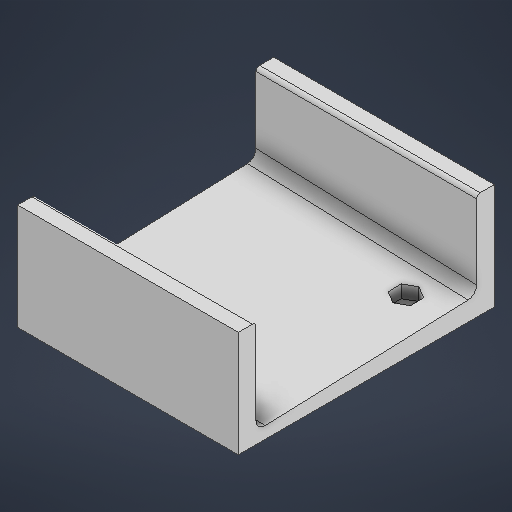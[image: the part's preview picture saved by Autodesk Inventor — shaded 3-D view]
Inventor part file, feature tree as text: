
AUTODESK INVENTOR PART (.ipt)
format: ipt  version: 2025.1 (Build 291241020, 241B)  size: 284,672 bytes
history: native  units: in
note: dims shown in document units (in); Inventor stores cm internally (conversion verified against a paired STEP export)
features: extrude x5, sketch x5, plane x2, fillet x2, projected_geometry x2
ambient origin geometry x8: Origin, YZ Plane, XZ Plane, XY Plane, X Axis, Y Axis, Z Axis, Center Point
bodies: Solid1 (feature_tree)
feature tree (16):
  extrude  "Extrusion1"  Depth=3.62in
  plane  "Work Plane3"
  sketch  "Sketch4"  dims[d2=0.125in d3=0.25in d4=0.125in]
  extrude  "Extrusion2"  Depth=0.25in
  fillet  "Fillet1"  Radius=0.125in
  plane  "Work Plane4"
  extrude  "Extrusion3"  Depth=1.5in TaperAngle=0.0deg
  extrude  "Extrusion4"  Depth=0.4in
  extrude  "Extrusion5"  Depth=0.05in
  fillet  "Fillet3"  [1 undecoded]
  sketch  "Sketch1"  dims[d0=3.37in d1=3.62in]
  projected_geometry  "Projected Loop1"
  projected_geometry  "Projected Loop2"
  sketch  "Sketch5"  dims[d5=0.25in d6=1.5in d7=0.0in]
  sketch  "Sketch6"  dims[d34=45.0deg d35=0.4in]
  sketch  "Sketch7"  dims[d36=0.0in d37=0.0in d38=0.05in d39=-0.29in d42=0.318in d43=0.5in d45=0.318in d46=0.189in d47=0.0in d48=0.15in d49=1.217in d50=0.14in d51=0.14in d52=0.189in d53=0.0in d55=0.125in d56=0.125in d57=1.5in d58=0.0in d59=0.5in d61=0.5in d62=0.5in d63=0.5in d64=0.125in]
note: 1 required parameter value undecoded (feature->parameter linkage not recoverable at this tier; creation-order binding heuristic only, values carry confidence <= 0.55)
